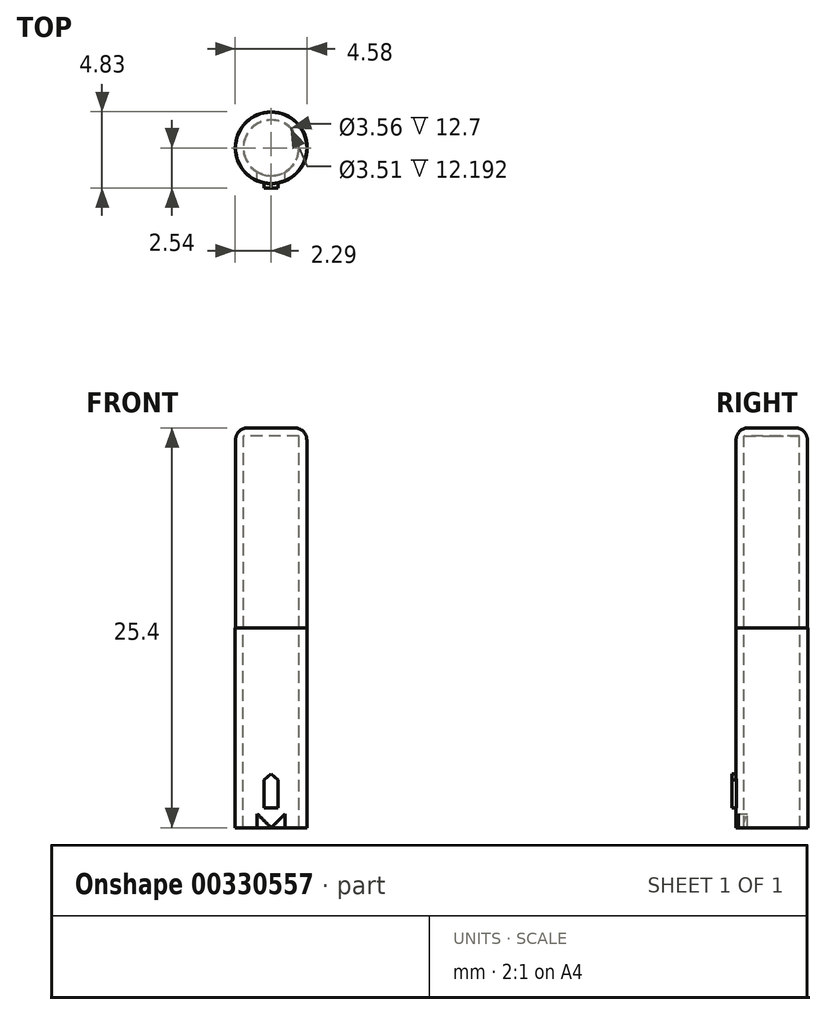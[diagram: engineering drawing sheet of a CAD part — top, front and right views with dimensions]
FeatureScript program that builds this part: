
annotation { "Feature Type Name" : "Feature", "Feature Type Description" : "" }
export const myFeature = defineFeature(function(context is Context, id is Id, definition is map)
    precondition{}
    {
        {
            var Q0;
            Q0=qCreatedBy(makeId("Front.planeOp"),FACE);
            var sketch = newSketch(context, id + "F0", { "sketchPlane" : qUnion([Q0])});
            skLineSegment(sketch, "E0", {"start": v(0, 0) * mm, "end": v(0, 25.4) * mm});
            skLineSegment(sketch, "E1", {"start": v(0, 0) * mm, "end": v(2.29, 0) * mm});
            skLineSegment(sketch, "E2", {"start": v(2.29, 0) * mm, "end": v(2.29, 12.7) * mm});
            skLineSegment(sketch, "E3", {"start": v(2.29, 12.7) * mm, "end": v(2.26, 12.7) * mm});
            skLineSegment(sketch, "E4", {"start": v(2.26, 12.7) * mm, "end": v(2.26, 25.4) * mm});
            skLineSegment(sketch, "E5", {"start": v(2.26, 25.4) * mm, "end": v(0, 25.4) * mm});
            skLineSegment(sketch, "E6.0", {"start": v(1.78, 0) * mm, "end": v(1.78, 12.7) * mm});
            skLineSegment(sketch, "E6.1", {"start": v(1.75, 12.7) * mm, "end": v(1.75, 24.9) * mm});
            skLineSegment(sketch, "E6.2", {"start": v(1.75, 24.9) * mm, "end": v(0, 24.9) * mm});
            skLineSegment(sketch, "E7", {"start": v(1.78, 12.7) * mm, "end": v(1.75, 12.7) * mm});
            skSolve(sketch);
        }
        {
            var Q0;
            {var subQ0=sQuery(id+"F0.wireOp",EDGE,"E2");Q0=makeQuery(id+"F0.imprint","IMPRINT",FACE,{"disambiguationData":[TD([[makeQuery(id+"F0.imprint","IMPRINT",EDGE,{"derivedFrom":subQ0}),1.0]])]});}
            var Q1;
            {var subQ0=sQuery(id+"F0.wireOp",EDGE,"E6.0");Q1=makeQuery(id+"F0.imprint","IMPRINT",FACE,{"disambiguationData":[TD([[makeQuery(id+"F0.imprint","IMPRINT",EDGE,{"derivedFrom":subQ0}),1.0]])]});}
            var Q2;
            Q2=sQuery(id+"F0.wireOp",EDGE,"E0");
            revolve(context, id + "F1", {"entities" : qUnion([Q0, Q1]), "axis" : qUnion([Q2]), "revolveType" : RevolveType.FULL});
        }
        {
            var Q0;
            Q0=qCreatedBy(makeId("Front.planeOp"),FACE);
            var sketch = newSketch(context, id + "F2", { "sketchPlane" : qUnion([Q0])});
            skLineSegment(sketch, "E8.bottom", {"start": v(-0.44, 1.27) * mm, "end": v(0.44, 1.27) * mm});
            skLineSegment(sketch, "E8.left", {"start": v(-0.44, 1.27) * mm, "end": v(-0.44, 3.05) * mm});
            skLineSegment(sketch, "E8.right", {"start": v(0.44, 1.27) * mm, "end": v(0.44, 3.05) * mm});
            skPoint(sketch, "E9", {"position": v(0, 1.27) * mm});
            skLineSegment(sketch, "E10", {"start": v(-0.44, 3.05) * mm, "end": v(0, 3.43) * mm});
            skLineSegment(sketch, "E11", {"start": v(0, 3.43) * mm, "end": v(0.44, 3.05) * mm});
            skLineSegment(sketch, "E12", {"start": v(-0.44, 0.44) * mm, "end": v(0, 0) * mm});
            skLineSegment(sketch, "E13", {"start": v(0, 0) * mm, "end": v(0.44, 0.44) * mm});
            skLineSegment(sketch, "E14", {"start": v(-0.44, 0) * mm, "end": v(0.44, 0) * mm});
            skLineSegment(sketch, "E15", {"start": v(0.44, 0.44) * mm, "end": v(0.89, 0.89) * mm});
            skLineSegment(sketch, "E16", {"start": v(0.89, 0.89) * mm, "end": v(0.89, 0) * mm});
            skLineSegment(sketch, "E17", {"start": v(0.89, 0) * mm, "end": v(0.44, 0) * mm});
            skLineSegment(sketch, "E18", {"start": v(-0.44, 0.44) * mm, "end": v(-0.89, 0.89) * mm});
            skLineSegment(sketch, "E19", {"start": v(-0.89, 0.89) * mm, "end": v(-0.89, 0) * mm});
            skLineSegment(sketch, "E20", {"start": v(-0.89, 0) * mm, "end": v(-0.44, 0) * mm});
            skSolve(sketch);
        }
        {
            var Q0;
            Q0=makeQuery(id+"F2.imprint","IMPRINT",FACE,{"disambiguationData":[TD([[makeQuery(id+"F2.imprint","IMPRINT",EDGE,{"derivedFrom":sQuery(id+"F2.wireOp",EDGE,"E8.bottom")}),1.0]])]});
            var Q1;
            Q1=makeQuery(id+"F1.opRevolve","SWEPT_FACE",FACE,{"disambiguationData":[OSD([sQuery(id+"F0.wireOp",EDGE,"E2")])]});
            var Q2;
            Q2=makeQuery(id+"F1.opRevolve","SWEPT_FACE",FACE,{"disambiguationData":[OSD([sQuery(id+"F0.wireOp",EDGE,"E2")])]});
            extrude(context, id + "F3", {"entities" : qUnion([Q0]), "operationType" : NewBodyOperationType.ADD, "endBoundEntityFace" : qUnion([Q1]), "depth" : 2.54 * mm});
        }
        {
            var Q0;
            {var subQ1=sQuery(id+"F2.wireOp",EDGE,"E12");Q0=makeQuery(id+"F2.imprint","IMPRINT",FACE,{"disambiguationData":[TD([[makeQuery(id+"F2.imprint","IMPRINT",EDGE,{"derivedFrom":subQ1}),-1.0]])]});}
            var Q1;
            {var subQ1=sQuery(id+"F2.wireOp",EDGE,"E13");Q1=makeQuery(id+"F2.imprint","IMPRINT",FACE,{"disambiguationData":[TD([[makeQuery(id+"F2.imprint","IMPRINT",EDGE,{"derivedFrom":subQ1}),-1.0]])]});}
            var Q2;
            Q2=makeQuery(id+"F1.opRevolve","SWEPT_FACE",FACE,{"disambiguationData":[OSD([sQuery(id+"F0.wireOp",EDGE,"E2")])]});
            extrude(context, id + "F4", {"entities" : qUnion([Q0, Q1]), "operationType" : NewBodyOperationType.REMOVE, "endBound" : BoundingType.UP_TO_SURFACE, "endBoundEntityFace" : qUnion([Q2]), "depth" : 25.4 * mm});
        }
        {
            var Q0;
            {var subQ0=sQuery(id+"F0.wireOp",EDGE,"E6.0");Q0=makeQuery(id+"F0.imprint","IMPRINT",FACE,{"disambiguationData":[TD([[makeQuery(id+"F0.imprint","IMPRINT",EDGE,{"derivedFrom":subQ0}),1.0]])]});}
            var Q1;
            Q1=sQuery(id+"F0.wireOp",EDGE,"E0");
            revolve(context, id + "F5", {"operationType" : NewBodyOperationType.REMOVE, "entities" : qUnion([Q0]), "axis" : qUnion([Q1]), "revolveType" : RevolveType.FULL, "oppositeDirection" : true});
        }
        {
            var Q0;
            Q0=makeQuery(id+"F1.opRevolve","SWEPT_EDGE",EDGE,{"disambiguationData":[OSD([sQuery(id+"F0.wireOp",EDGE,"E4"),sQuery(id+"F0.wireOp",EDGE,"E5")])]});
            fillet(context, id + "F6", {"entities" : qUnion([Q0]), "radius" : 0.76 * mm, "tangentPropagation" : true, "allowEdgeOverflow" : false});
        }
    });
